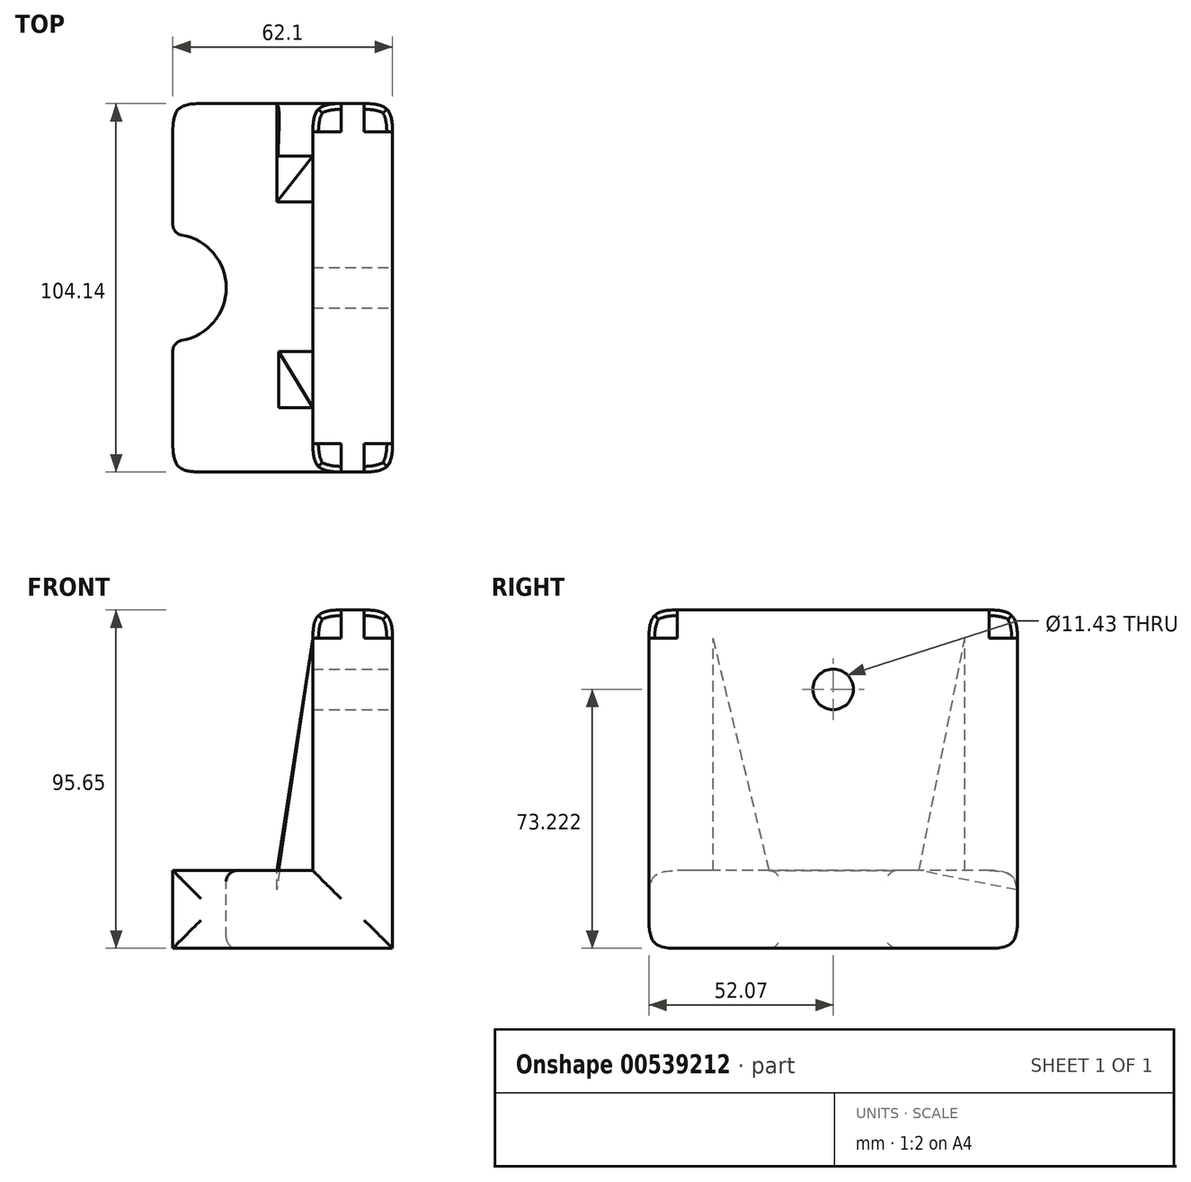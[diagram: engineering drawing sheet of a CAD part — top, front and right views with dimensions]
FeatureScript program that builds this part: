
annotation { "Feature Type Name" : "Feature", "Feature Type Description" : "" }
export const myFeature = defineFeature(function(context is Context, id is Id, definition is map)
    precondition{}
    {
        {
            var Q0;
            Q0=qCreatedBy(makeId("Front.planeOp"),FACE);
            var sketch = newSketch(context, id + "F0", { "sketchPlane" : qUnion([Q0])});
            skLineSegment(sketch, "E0", {"start": v(-25.42, -42.46) * mm, "end": v(36.68, -42.46) * mm});
            skLineSegment(sketch, "E1", {"start": v(36.68, -42.46) * mm, "end": v(36.68, 53.2) * mm});
            skLineSegment(sketch, "E2", {"start": v(36.68, 53.2) * mm, "end": v(14.15, 53.2) * mm});
            skLineSegment(sketch, "E3", {"start": v(14.15, 53.2) * mm, "end": v(14.15, -20.46) * mm});
            skLineSegment(sketch, "E4", {"start": v(14.15, -20.46) * mm, "end": v(-25.42, -20.46) * mm});
            skLineSegment(sketch, "E5", {"start": v(-25.42, -42.46) * mm, "end": v(-25.42, -20.46) * mm});
            skSolve(sketch);
        }
        {
            var Q0;
            Q0=makeQuery(id+"F0.imprint","IMPRINT",FACE,{"disambiguationData":[TD([[makeQuery(id+"F0.imprint","IMPRINT",EDGE,{"derivedFrom":sQuery(id+"F0.wireOp",EDGE,"E0")}),1.0]])]});
            extrude(context, id + "F1", {"entities" : qUnion([Q0]), "endBound" : BoundingType.SYMMETRIC, "oppositeDirection" : true, "depth" : 104.14 * mm, "offsetDistance" : 25.4 * mm});
        }
        {
            var Q0;
            Q0=makeQuery(id+"F1.opExtrude","SWEPT_FACE",FACE,{"disambiguationData":[OSD([sQuery(id+"F0.wireOp",EDGE,"E1")])]});
            var sketch = newSketch(context, id + "F2", { "sketchPlane" : qUnion([Q0])});
            skCircle(sketch, "E6", {"center": v(0, 30.76) * mm, "radius": 13.62 * mm});
            skCircle(sketch, "E7", {"center": v(0, 30.76) * mm, "radius": 5.71 * mm});
            skSolve(sketch);
        }
        {
            var Q0;
            Q0=makeQuery(id+"F1.opExtrude","CAP_FACE",FACE,{"disambiguationData":[OSD([sQuery(id+"F0.wireOp",EDGE,"E0"),sQuery(id+"F0.wireOp",EDGE,"E1"),sQuery(id+"F0.wireOp",EDGE,"E2"),sQuery(id+"F0.wireOp",EDGE,"E3"),sQuery(id+"F0.wireOp",EDGE,"E4"),sQuery(id+"F0.wireOp",EDGE,"E5")])],"isStart":true});
            var Q1;
            Q1=makeQuery(id+"F1.opExtrude","SWEPT_FACE",FACE,{"disambiguationData":[OSD([sQuery(id+"F0.wireOp",EDGE,"E2")])]});
            var Q2;
            Q2=makeQuery(id+"F1.opExtrude","CAP_FACE",FACE,{"disambiguationData":[OSD([sQuery(id+"F0.wireOp",EDGE,"E0"),sQuery(id+"F0.wireOp",EDGE,"E1"),sQuery(id+"F0.wireOp",EDGE,"E2"),sQuery(id+"F0.wireOp",EDGE,"E3"),sQuery(id+"F0.wireOp",EDGE,"E4"),sQuery(id+"F0.wireOp",EDGE,"E5")])],"isStart":false});
            fillet(context, id + "F3", {"entities" : qUnion([Q0, Q1, Q2]), "radius" : 7.97 * mm, "tangentPropagation" : true, "rho" : 0.6, "crossSection" : FilletCrossSection.CONIC, "allowEdgeOverflow" : false});
        }
        {
            var Q0;
            Q0=makeQuery(id+"F2.imprint","IMPRINT",FACE,{"disambiguationData":[TD([[makeQuery(id+"F2.imprint","IMPRINT",EDGE,{"derivedFrom":sQuery(id+"F2.wireOp",EDGE,"E7")}),1.0]])]});
            var Q1;
            Q1=sQuery(id+"F2.wireOp",EDGE,"E7");
            extrude(context, id + "F4", {"entities" : qUnion([Q0]), "operationType" : NewBodyOperationType.REMOVE, "surfaceEntities" : qUnion([Q1]), "oppositeDirection" : true, "depth" : 38.6 * mm, "offsetDistance" : 25.4 * mm});
        }
        {
            var Q0;
            Q0=makeQuery(id+"F1.opExtrude","SWEPT_FACE",FACE,{"disambiguationData":[OSD([sQuery(id+"F0.wireOp",EDGE,"E4")])]});
            var sketch = newSketch(context, id + "F5", { "sketchPlane" : qUnion([Q0])});
            skCircle(sketch, "E8", {"center": v(-25.42, 0) * mm, "radius": 15.1 * mm});
            skSolve(sketch);
        }
        {
            var Q0;
            {var subQ0=sQuery(id+"F5.wireOp",EDGE,"E8");var subQ1=makeQuery(id+"F1.opExtrude","SWEPT_EDGE",EDGE,{"disambiguationData":[OSD([sQuery(id+"F0.wireOp",EDGE,"E4"),sQuery(id+"F0.wireOp",EDGE,"E5")])]});var subQ2=makeQuery(id+"F5.imprint","INTERSECT",VERTEX,{"disambiguationData":[OD(0.0)],"derivedFrom":[subQ1,subQ0]});Q0=makeQuery(id+"F5.imprint","IMPRINT",FACE,{"disambiguationData":[TD([[makeQuery(id+"F5.imprint","IMPRINT",EDGE,{"disambiguationData":[TD([[subQ2,-1.0]])],"derivedFrom":subQ0}),1.0]])]});}
            extrude(context, id + "F6", {"entities" : qUnion([Q0]), "operationType" : NewBodyOperationType.REMOVE, "oppositeDirection" : true, "depth" : 62.23 * mm, "offsetDistance" : 25.4 * mm});
        }
        {
            var Q0;
            Q0=makeQuery(id+"F1.opExtrude","SWEPT_FACE",FACE,{"disambiguationData":[OSD([sQuery(id+"F0.wireOp",EDGE,"E3")])]});
            var sketch = newSketch(context, id + "F7", { "sketchPlane" : qUnion([Q0])});
            skLineSegment(sketch, "E9", {"start": v(33.88, 45.22) * mm, "end": v(33.88, -20.46) * mm});
            skLineSegment(sketch, "E10", {"start": v(33.88, 45.22) * mm, "end": v(18.06, -20.46) * mm});
            skLineSegment(sketch, "E11", {"start": v(18.06, -20.46) * mm, "end": v(33.88, -20.46) * mm});
            skSolve(sketch);
        }
        {
            var Q0;
            Q0 = qSketchRegion(id + "F7", true);
            extrude(context, id + "F8", {"entities" : qUnion([Q0]), "operationType" : NewBodyOperationType.ADD, "endBound" : BoundingType.SYMMETRIC, "depth" : 19.3 * mm, "offsetDistance" : 25.4 * mm});
        }
        {
            var Q0;
            {var subQ0=sQuery(id+"F0.wireOp",EDGE,"E3");var subQ3=makeQuery(id+"F1.opExtrude","SWEPT_FACE",FACE,{"disambiguationData":[OSD([subQ0])]});Q0=makeQuery(id+"F8.boolean.opBoolean","SPLIT",FACE,{"disambiguationData":[TD([makeQuery(id+"F4.boolean.opBoolean","COPY",FACE,{"derivedFrom":makeQuery(id+"F4.opExtrude","SWEPT_FACE",FACE,{"disambiguationData":[OSD([sQuery(id+"F2.wireOp",EDGE,"E7")])]})})])],"derivedFrom":subQ3});}
            var sketch = newSketch(context, id + "F9", { "sketchPlane" : qUnion([Q0])});
            skLineSegment(sketch, "E12", {"start": v(-37.21, 45.22) * mm, "end": v(-37.21, -20.46) * mm});
            skLineSegment(sketch, "E13", {"start": v(-37.21, 45.22) * mm, "end": v(-24.27, -20.46) * mm});
            skLineSegment(sketch, "E14", {"start": v(-37.21, -20.46) * mm, "end": v(-24.27, -20.46) * mm});
            skSolve(sketch);
        }
        {
            var Q0;
            Q0=makeQuery(id+"F8.opExtrude","SWEPT_FACE",FACE,{"disambiguationData":[OSD([sQuery(id+"F7.wireOp",EDGE,"E9")])]});
            var sketch = newSketch(context, id + "F10", { "sketchPlane" : qUnion([Q0])});
            skLineSegment(sketch, "E15", {"start": v(4.5, -20.46) * mm, "end": v(14.15, 45.22) * mm});
            skLineSegment(sketch, "E16", {"start": v(14.15, 45.22) * mm, "end": v(4.5, 45.22) * mm});
            skLineSegment(sketch, "E17", {"start": v(4.5, 45.22) * mm, "end": v(4.5, -20.46) * mm});
            skSolve(sketch);
        }
        {
            var Q0;
            Q0 = qSketchRegion(id + "F10", true);
            extrude(context, id + "F11", {"entities" : qUnion([Q0]), "operationType" : NewBodyOperationType.REMOVE, "oppositeDirection" : true, "depth" : 409.7 * mm, "offsetDistance" : 25.4 * mm});
        }
        {
            var Q0;
            Q0=makeQuery(id+"F9.imprint","IMPRINT",FACE,{"disambiguationData":[TD([[makeQuery(id+"F9.imprint","IMPRINT",EDGE,{"derivedFrom":sQuery(id+"F9.wireOp",EDGE,"E12")}),1.0]])]});
            extrude(context, id + "F12", {"entities" : qUnion([Q0]), "operationType" : NewBodyOperationType.ADD, "endBound" : BoundingType.SYMMETRIC, "depth" : 20.32 * mm, "offsetDistance" : 25.4 * mm});
        }
        {
            var Q0;
            Q0=makeQuery(id+"F12.opExtrude","SWEPT_FACE",FACE,{"disambiguationData":[OSD([sQuery(id+"F9.wireOp",EDGE,"E13")])]});
            var sketch = newSketch(context, id + "F13", { "sketchPlane" : qUnion([Q0])});
            skLineSegment(sketch, "E18", {"start": v(4, -15.38) * mm, "end": v(14.15, 51.56) * mm});
            skLineSegment(sketch, "E19", {"start": v(4, 51.56) * mm, "end": v(4, -15.38) * mm});
            skSolve(sketch);
        }
        {
            var Q0;
            Q0=makeQuery(id+"F13.imprint","IMPRINT",FACE,{"disambiguationData":[TD([[makeQuery(id+"F13.imprint","IMPRINT",EDGE,{"derivedFrom":sQuery(id+"F13.wireOp",EDGE,"E18")}),1.0]])]});
            extrude(context, id + "F14", {"entities" : qUnion([Q0]), "operationType" : NewBodyOperationType.REMOVE, "oppositeDirection" : true, "depth" : 104.4 * mm, "offsetDistance" : 25.4 * mm});
        }
        {
            var Q0;
            Q0=makeQuery(id+"F6.boolean.opBoolean","COPY",FACE,{"derivedFrom":makeQuery(id+"F6.opExtrude","SWEPT_FACE",FACE,{"disambiguationData":[OSD([sQuery(id+"F5.wireOp",EDGE,"E8")])]})});
            fillet(context, id + "F15", {"entities" : qUnion([Q0]), "radius" : 3.07 * mm, "tangentPropagation" : true, "allowEdgeOverflow" : false});
        }
    });
